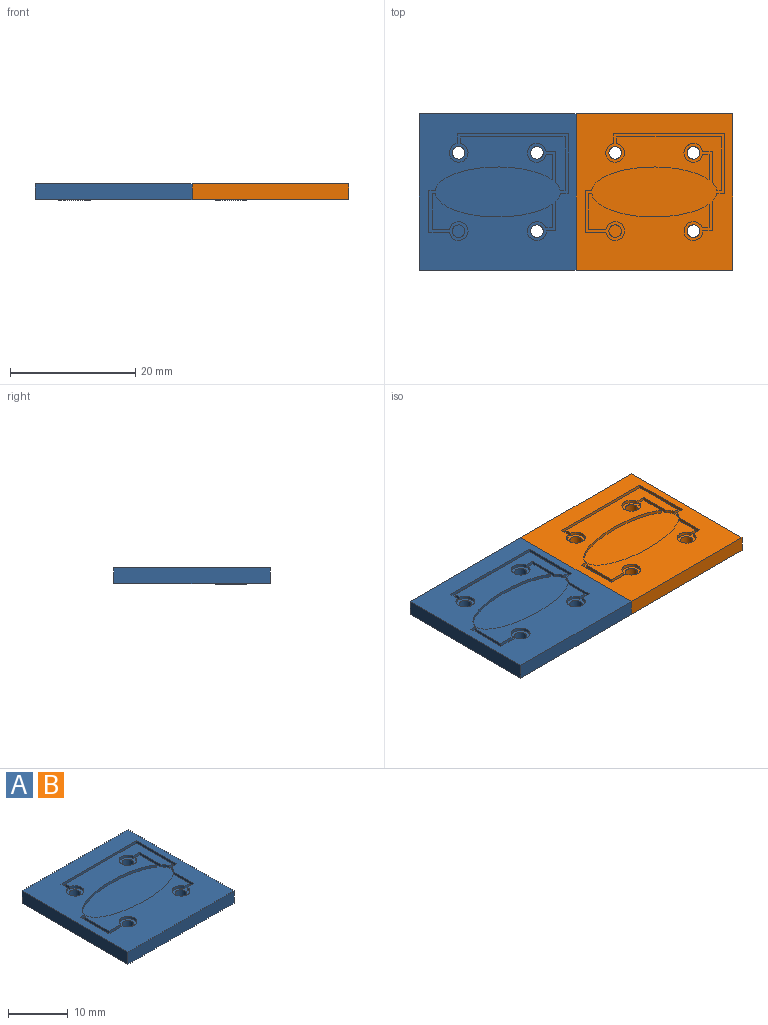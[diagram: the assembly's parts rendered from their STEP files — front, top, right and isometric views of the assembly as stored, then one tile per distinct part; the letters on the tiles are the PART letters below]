
ASSEMBLY  parts=2 mates=1
PART A: 44 faces, bbox 25x25x2.6 mm
  f0: plane 22.24x17.05mm, normal (0,0,1), area 166.5mm2, adj f5,f6,f7,f8,f9,f10,f11,f12
  f1: plane 25x25mm, normal (0,0,-1), area 595.9mm2, adj f2,f3,f4,f35,f37,f38,f40,f42
  f2: plane 25x2.5mm, normal (0,1,0), area 62.5mm2, adj f1,f3,f35,f36
  f3: plane 25x2.5mm, normal (-1,0,0), area 62.5mm2, adj f1,f2,f4,f36
  f4: plane 25x2.5mm, normal (0,-1,0), area 62.5mm2, adj f1,f3,f35,f36
  f5: extruded ~1.27x0.73mm, area 0.7mm2, adj f0,f6,f34,f36
  f6: plane 0.76x0.5mm, normal (0,-1,0), area 0.4mm2, adj f0,f5,f7,f36
  f7: plane 8.55x0.5mm, normal (1,0,0), area 4.3mm2, adj f0,f6,f8,f36
  f8: plane 16.74x0.5mm, normal (0,1,0), area 8.4mm2, adj f0,f7,f9,f36
  f9: plane 1.07x0.5mm, normal (-1,0,0), area 0.5mm2, adj f0,f8,f10,f36
  f10: cylinder r=1.5mm len=3mm, axis (0,0,-1), area 4.5mm2, adj f0,f9,f11,f36
  f11: plane 1.57x0.5mm, normal (1,0,0), area 0.8mm2, adj f0,f10,f12,f36
  f12: plane 17.74x0.5mm, normal (0,-1,0), area 8.9mm2, adj f0,f11,f13,f36
  f13: plane 9.55x0.5mm, normal (-1,0,0), area 4.8mm2, adj f0,f12,f14,f36
  f14: plane 1.26x0.5mm, normal (0,1,0), area 0.6mm2, adj f0,f13,f15,f36
  f15: extruded ~1.27x0.73mm, area 0.7mm2, adj f0,f14,f16,f36
  f16: plane 4.7x0.5mm, normal (-1,0,0), area 2.3mm2, adj f0,f15,f17,f36
  f17: plane 1.5x0.5mm, normal (0,1,0), area 0.8mm2, adj f0,f16,f18,f36
  f18: cylinder r=1.5mm len=3mm, axis (0,0,-1), area 4.5mm2, adj f0,f17,f19,f36
  f19: plane 1.1x0.5mm, normal (0,-1,0), area 0.5mm2, adj f0,f18,f20,f36
  f20: plane 3.78x0.5mm, normal (1,0,0), area 1.9mm2, adj f0,f19,f21,f36
  f21: extruded ~18.73x3.75mm, area 10.2mm2, adj f0,f20,f22,f36
  f22: plane 0.5x0.49mm, normal (0,1,0), area 0.2mm2, adj f0,f21,f23,f36
  f23: plane 5.75x0.5mm, normal (-1,0,0), area 2.9mm2, adj f0,f22,f24,f36
  f24: plane 2.74x0.5mm, normal (0,-1,0), area 1.4mm2, adj f0,f23,f25,f36
  f25: cylinder r=1.5mm len=3mm, axis (0,0,-1), area 4.5mm2, adj f0,f24,f26,f36
  f26: plane 3.26x0.5mm, normal (0,1,0), area 1.6mm2, adj f0,f25,f27,f36
  f27: plane 6.75x0.5mm, normal (1,0,0), area 3.4mm2, adj f0,f26,f28,f36
  f28: plane 1.01x0.5mm, normal (0,-1,0), area 0.5mm2, adj f0,f27,f29,f36
  f29: extruded ~18.73x3.75mm, area 10.2mm2, adj f0,f28,f30,f36
  f30: plane 4.06x0.5mm, normal (1,0,0), area 2mm2, adj f0,f29,f31,f36
  f31: plane 1.02x0.5mm, normal (0,1,0), area 0.5mm2, adj f0,f30,f32,f36
  f32: cylinder r=1.5mm len=3mm, axis (0,0,-1), area 4.5mm2, adj f0,f31,f33,f36
  f33: plane 1.52x0.5mm, normal (0,-1,0), area 0.8mm2, adj f0,f32,f34,f36
  f34: plane 4.98x0.5mm, normal (-1,0,0), area 2.5mm2, adj f0,f5,f33,f36
  f35: plane 25x2.5mm, normal (1,0,0), area 62.5mm2, adj f1,f2,f4,f36
  f36: plane 25x25mm, normal (0,0,1), area 446mm2, adj f2,f3,f4,f5,f6,f7,f8,f9
  f37: cylinder r=1mm len=2mm, axis (0,0,1), area 12.6mm2, adj f0,f1
  f38: cylinder r=1mm len=2mm, axis (0,0,1), area 12.6mm2, adj f0,f1
  f39: cylinder r=1mm len=2mm, axis (0,0,1), area 12.6mm2, adj f0,f43
  f40: cylinder r=1mm len=2mm, axis (0,0,1), area 12.6mm2, adj f0,f1
  f41: plane 5x5mm, normal (0,0,-1), area 19.6mm2, adj f42
  f42: cylinder r=2.5mm len=5mm, axis (0,0,1), area 1.6mm2, adj f1,f41
  f43: plane 2x2mm, normal (0,0,1), area 3.1mm2, adj f39
PART B: same geometry as A
PLACE A t=(-6.54,5.86,-6.4)mm
PLACE B t=(18.46,5.86,-6.4)mm
MATE fastened A.f35 <-> B.f3  axis (1,0,0) through (5.96,5.86,-7.15)mm
